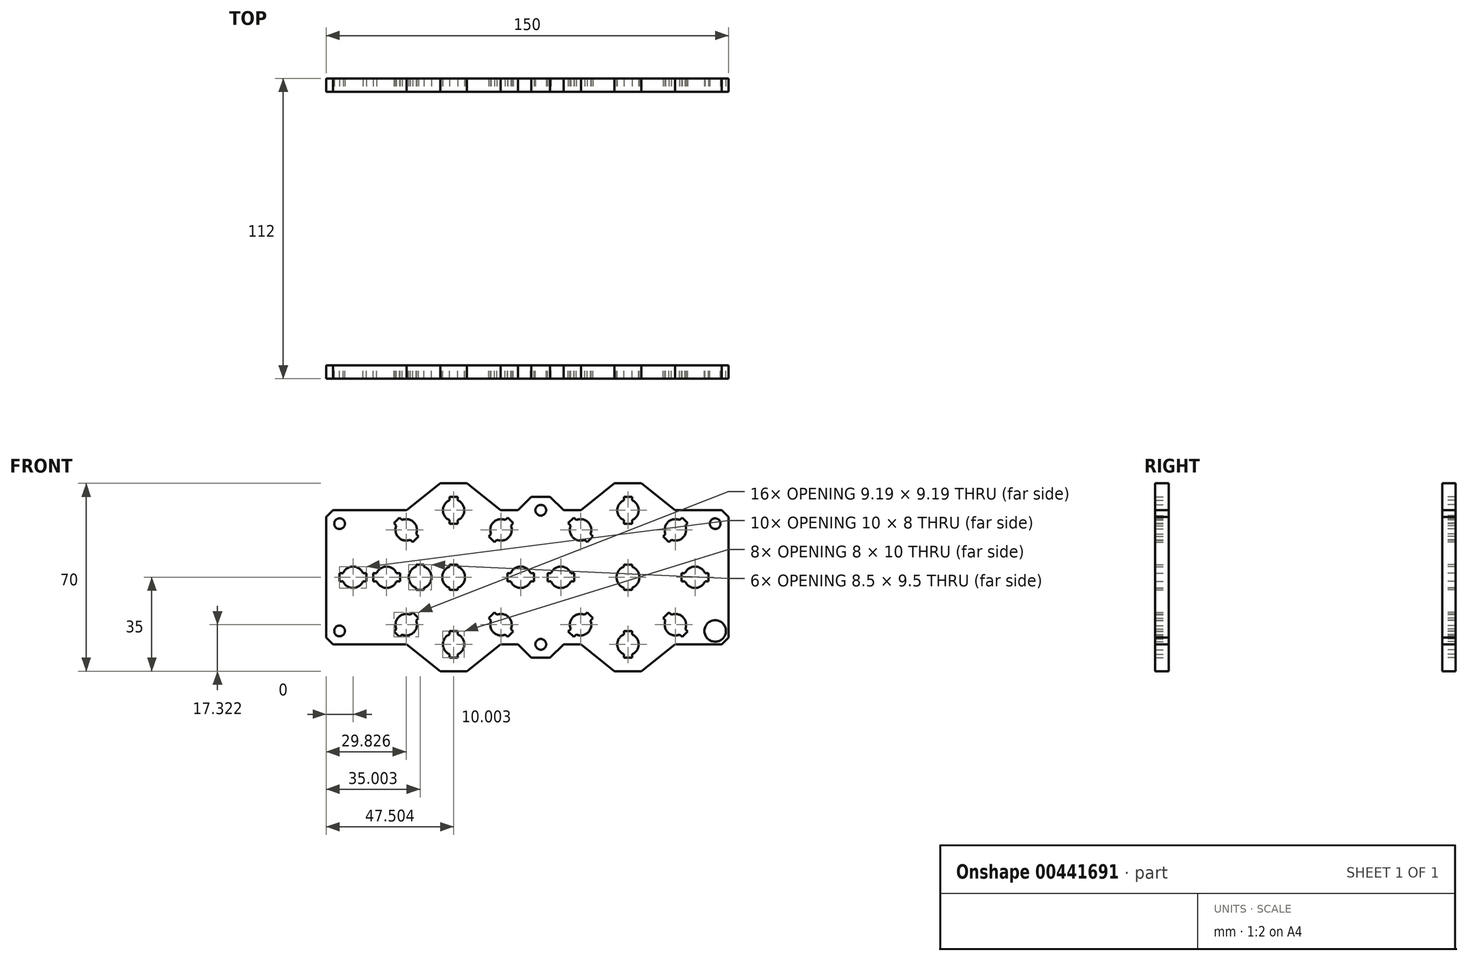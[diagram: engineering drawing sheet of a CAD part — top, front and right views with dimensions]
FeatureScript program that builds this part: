
annotation { "Feature Type Name" : "Feature", "Feature Type Description" : "" }
export const myFeature = defineFeature(function(context is Context, id is Id, definition is map)
    precondition{}
    {
        {
            var Q0;
            Q0=qCreatedBy(makeId("Front.planeOp"),FACE);
            var sketch = newSketch(context, id + "F0", { "sketchPlane" : qUnion([Q0])});
            skLineSegment(sketch, "E0", {"start": v(-68.44, 0) * mm, "end": v(-68.44, 25) * mm});
            skLineSegment(sketch, "E1", {"start": v(-68.44, 25) * mm, "end": v(-38.44, 25) * mm});
            skLineSegment(sketch, "E2", {"start": v(-38.44, 25) * mm, "end": v(-25.94, 35) * mm});
            skLineSegment(sketch, "E3", {"start": v(-25.94, 35) * mm, "end": v(-15.94, 35) * mm});
            skLineSegment(sketch, "E4", {"start": v(-15.94, 35) * mm, "end": v(-3.44, 25) * mm});
            skLineSegment(sketch, "E5", {"start": v(-3.44, 25) * mm, "end": v(26.56, 25) * mm});
            skLineSegment(sketch, "E6", {"start": v(26.56, 25) * mm, "end": v(39.06, 35) * mm});
            skLineSegment(sketch, "E7", {"start": v(39.06, 35) * mm, "end": v(49.06, 35) * mm});
            skLineSegment(sketch, "E8", {"start": v(49.06, 35) * mm, "end": v(61.56, 25) * mm});
            skLineSegment(sketch, "E9", {"start": v(61.56, 25) * mm, "end": v(81.56, 25) * mm});
            skLineSegment(sketch, "E10", {"start": v(81.56, 25) * mm, "end": v(81.56, 0) * mm});
            skLineSegment(sketch, "E11", {"start": v(-20.94, 68.31) * mm, "end": v(-20.94, -69.34) * mm, "construction": true});
            skLineSegment(sketch, "E12", {"start": v(44.06, 67.89) * mm, "end": v(44.06, -61.73) * mm, "construction": true});
            skLineSegment(sketch, "E13", {"start": v(87.46, 0) * mm, "end": v(-83.25, 0) * mm, "construction": true});
            skCircle(sketch, "E14", {"center": v(-20.94, 25) * mm, "radius": 4 * mm});
            skCircle(sketch, "E15", {"center": v(-20.94, 0) * mm, "radius": 25 * mm, "construction": true});
            skLineSegment(sketch, "E16", {"start": v(11.56, 59.14) * mm, "end": v(11.56, -51.84) * mm, "construction": true});
            skCircle(sketch, "E17.MirrorC", {"center": v(44.06, 0) * mm, "radius": 25 * mm, "construction": true});
            skCircle(sketch, "E18.MirrorC", {"center": v(44.06, 25) * mm, "radius": 4 * mm});
            skCircle(sketch, "E19.1.0", {"center": v(-38.61, 17.68) * mm, "radius": 4 * mm});
            skCircle(sketch, "E19.2.0", {"center": v(-45.94, 0) * mm, "radius": 4 * mm});
            skCircle(sketch, "E19.3.0", {"center": v(-38.61, -17.68) * mm, "radius": 4 * mm});
            skCircle(sketch, "E19.4.0", {"center": v(-20.94, -25) * mm, "radius": 4 * mm});
            skCircle(sketch, "E19.5.0", {"center": v(-3.26, -17.68) * mm, "radius": 4 * mm});
            skCircle(sketch, "E19.6.0", {"center": v(4.06, 0) * mm, "radius": 4 * mm});
            skCircle(sketch, "E19.7.0", {"center": v(-3.26, 17.68) * mm, "radius": 4 * mm});
            skCircle(sketch, "E20.MirrorC", {"center": v(61.74, 17.68) * mm, "radius": 4 * mm});
            skCircle(sketch, "E21.MirrorC", {"center": v(69.06, 0) * mm, "radius": 4 * mm});
            skCircle(sketch, "E22.MirrorC", {"center": v(61.74, -17.68) * mm, "radius": 4 * mm});
            skCircle(sketch, "E23.MirrorC", {"center": v(44.06, -25) * mm, "radius": 4 * mm});
            skCircle(sketch, "E24.MirrorC", {"center": v(26.39, -17.68) * mm, "radius": 4 * mm});
            skCircle(sketch, "E25.MirrorC", {"center": v(19.06, 0) * mm, "radius": 4 * mm});
            skCircle(sketch, "E26.MirrorC", {"center": v(26.39, 17.68) * mm, "radius": 4 * mm});
            skLineSegment(sketch, "E27.bottom", {"start": v(-22.44, 30) * mm, "end": v(-19.44, 30) * mm});
            skLineSegment(sketch, "E27.top", {"start": v(-22.44, 20) * mm, "end": v(-19.44, 20) * mm});
            skLineSegment(sketch, "E27.left", {"start": v(-22.44, 30) * mm, "end": v(-22.44, 20) * mm});
            skLineSegment(sketch, "E27.right", {"start": v(-19.44, 30) * mm, "end": v(-19.44, 20) * mm});
            skLineSegment(sketch, "E28", {"start": v(-32.15, 25) * mm, "end": v(-5.88, 25) * mm, "construction": true});
            skLineSegment(sketch, "E29.1.0", {"start": v(-43.21, 20.15) * mm, "end": v(-41.09, 22.27) * mm});
            skLineSegment(sketch, "E29.1.1", {"start": v(-43.21, 20.15) * mm, "end": v(-36.14, 13.08) * mm});
            skLineSegment(sketch, "E29.1.2", {"start": v(-36.14, 13.08) * mm, "end": v(-34.02, 15.2) * mm});
            skLineSegment(sketch, "E29.1.3", {"start": v(-41.09, 22.27) * mm, "end": v(-34.02, 15.2) * mm});
            skLineSegment(sketch, "E29.2.0", {"start": v(-50.94, -1.5) * mm, "end": v(-50.94, 1.5) * mm});
            skLineSegment(sketch, "E29.2.1", {"start": v(-50.94, -1.5) * mm, "end": v(-40.94, -1.5) * mm});
            skLineSegment(sketch, "E29.2.2", {"start": v(-40.94, -1.5) * mm, "end": v(-40.94, 1.5) * mm});
            skLineSegment(sketch, "E29.2.3", {"start": v(-50.94, 1.5) * mm, "end": v(-40.94, 1.5) * mm});
            skLineSegment(sketch, "E29.3.0", {"start": v(-41.09, -22.27) * mm, "end": v(-43.21, -20.15) * mm});
            skLineSegment(sketch, "E29.3.1", {"start": v(-41.09, -22.27) * mm, "end": v(-34.02, -15.2) * mm});
            skLineSegment(sketch, "E29.3.2", {"start": v(-34.02, -15.2) * mm, "end": v(-36.14, -13.08) * mm});
            skLineSegment(sketch, "E29.3.3", {"start": v(-43.21, -20.15) * mm, "end": v(-36.14, -13.08) * mm});
            skLineSegment(sketch, "E29.4.0", {"start": v(-19.44, -30) * mm, "end": v(-22.44, -30) * mm});
            skLineSegment(sketch, "E29.4.1", {"start": v(-19.44, -30) * mm, "end": v(-19.44, -20) * mm});
            skLineSegment(sketch, "E29.4.2", {"start": v(-19.44, -20) * mm, "end": v(-22.44, -20) * mm});
            skLineSegment(sketch, "E29.4.3", {"start": v(-22.44, -30) * mm, "end": v(-22.44, -20) * mm});
            skLineSegment(sketch, "E29.5.0", {"start": v(1.34, -20.15) * mm, "end": v(-0.78, -22.27) * mm});
            skLineSegment(sketch, "E29.5.1", {"start": v(1.34, -20.15) * mm, "end": v(-5.73, -13.08) * mm});
            skLineSegment(sketch, "E29.5.2", {"start": v(-5.73, -13.08) * mm, "end": v(-7.85, -15.2) * mm});
            skLineSegment(sketch, "E29.5.3", {"start": v(-0.78, -22.27) * mm, "end": v(-7.85, -15.2) * mm});
            skLineSegment(sketch, "E29.6.0", {"start": v(9.06, 1.5) * mm, "end": v(9.06, -1.5) * mm});
            skLineSegment(sketch, "E29.6.1", {"start": v(9.06, 1.5) * mm, "end": v(-0.94, 1.5) * mm});
            skLineSegment(sketch, "E29.6.2", {"start": v(-0.94, 1.5) * mm, "end": v(-0.94, -1.5) * mm});
            skLineSegment(sketch, "E29.6.3", {"start": v(9.06, -1.5) * mm, "end": v(-0.94, -1.5) * mm});
            skLineSegment(sketch, "E29.7.0", {"start": v(-0.78, 22.27) * mm, "end": v(1.34, 20.15) * mm});
            skLineSegment(sketch, "E29.7.1", {"start": v(-0.78, 22.27) * mm, "end": v(-7.85, 15.2) * mm});
            skLineSegment(sketch, "E29.7.2", {"start": v(-7.85, 15.2) * mm, "end": v(-5.73, 13.08) * mm});
            skLineSegment(sketch, "E29.7.3", {"start": v(1.34, 20.15) * mm, "end": v(-5.73, 13.08) * mm});
            skLineSegment(sketch, "E30.MirrorCS", {"start": v(45.56, 30) * mm, "end": v(42.56, 30) * mm});
            skLineSegment(sketch, "E31.MirrorCS", {"start": v(45.56, 30) * mm, "end": v(45.56, 20) * mm});
            skLineSegment(sketch, "E32.MirrorCS", {"start": v(45.56, 20) * mm, "end": v(42.56, 20) * mm});
            skLineSegment(sketch, "E33.MirrorCS", {"start": v(42.56, 30) * mm, "end": v(42.56, 20) * mm});
            skLineSegment(sketch, "E34.MirrorCS", {"start": v(23.91, 22.27) * mm, "end": v(30.98, 15.2) * mm});
            skLineSegment(sketch, "E35.MirrorCS", {"start": v(21.79, 20.15) * mm, "end": v(28.86, 13.08) * mm});
            skLineSegment(sketch, "E36.MirrorCS", {"start": v(30.98, 15.2) * mm, "end": v(28.86, 13.08) * mm});
            skLineSegment(sketch, "E37.MirrorCS", {"start": v(23.91, 22.27) * mm, "end": v(21.79, 20.15) * mm});
            skLineSegment(sketch, "E38.MirrorCS", {"start": v(-68.44, 0) * mm, "end": v(-68.44, -25) * mm});
            skLineSegment(sketch, "E39.MirrorCS", {"start": v(-68.44, -25) * mm, "end": v(-38.44, -25) * mm});
            skLineSegment(sketch, "E40.MirrorCS", {"start": v(-38.44, -25) * mm, "end": v(-25.94, -35) * mm});
            skLineSegment(sketch, "E41.MirrorCS", {"start": v(-25.94, -35) * mm, "end": v(-15.94, -35) * mm});
            skLineSegment(sketch, "E42.MirrorCS", {"start": v(-15.94, -35) * mm, "end": v(-3.44, -25) * mm});
            skLineSegment(sketch, "E43.MirrorCS", {"start": v(-3.44, -25) * mm, "end": v(26.56, -25) * mm});
            skLineSegment(sketch, "E44.MirrorCS", {"start": v(26.56, -25) * mm, "end": v(39.06, -35) * mm});
            skLineSegment(sketch, "E45.MirrorCS", {"start": v(39.06, -35) * mm, "end": v(49.06, -35) * mm});
            skLineSegment(sketch, "E46.MirrorCS", {"start": v(49.06, -35) * mm, "end": v(61.56, -25) * mm});
            skLineSegment(sketch, "E47.MirrorCS", {"start": v(61.56, -25) * mm, "end": v(81.56, -25) * mm});
            skLineSegment(sketch, "E48.MirrorCS", {"start": v(81.56, -25) * mm, "end": v(81.56, 0) * mm});
            skLineSegment(sketch, "E49.MirrorCS", {"start": v(14.06, 1.5) * mm, "end": v(24.06, 1.5) * mm});
            skLineSegment(sketch, "E50.MirrorCS", {"start": v(14.06, -1.5) * mm, "end": v(24.06, -1.5) * mm});
            skLineSegment(sketch, "E51.MirrorCS", {"start": v(14.06, 1.5) * mm, "end": v(14.06, -1.5) * mm});
            skLineSegment(sketch, "E52.MirrorCS", {"start": v(24.06, 1.5) * mm, "end": v(24.06, -1.5) * mm});
            skLineSegment(sketch, "E53.MirrorCS", {"start": v(28.86, -13.08) * mm, "end": v(30.98, -15.2) * mm});
            skLineSegment(sketch, "E54.MirrorCS", {"start": v(23.91, -22.27) * mm, "end": v(30.98, -15.2) * mm});
            skLineSegment(sketch, "E55.MirrorCS", {"start": v(21.79, -20.15) * mm, "end": v(28.86, -13.08) * mm});
            skLineSegment(sketch, "E56.MirrorCS", {"start": v(21.79, -20.15) * mm, "end": v(23.91, -22.27) * mm});
            skLineSegment(sketch, "E57.MirrorCS", {"start": v(42.56, -30) * mm, "end": v(45.56, -30) * mm});
            skLineSegment(sketch, "E58.MirrorCS", {"start": v(45.56, -30) * mm, "end": v(45.56, -20) * mm});
            skLineSegment(sketch, "E59.MirrorCS", {"start": v(42.56, -20) * mm, "end": v(45.56, -20) * mm});
            skLineSegment(sketch, "E60.MirrorCS", {"start": v(42.56, -30) * mm, "end": v(42.56, -20) * mm});
            skLineSegment(sketch, "E61.MirrorCS", {"start": v(64.22, -22.27) * mm, "end": v(57.15, -15.2) * mm});
            skLineSegment(sketch, "E62.MirrorCS", {"start": v(66.34, -20.15) * mm, "end": v(59.27, -13.08) * mm});
            skLineSegment(sketch, "E63.MirrorCS", {"start": v(64.22, -22.27) * mm, "end": v(66.34, -20.15) * mm});
            skLineSegment(sketch, "E64.MirrorCS", {"start": v(57.15, -15.2) * mm, "end": v(59.27, -13.08) * mm});
            skLineSegment(sketch, "E65.MirrorCS", {"start": v(74.06, -1.5) * mm, "end": v(64.06, -1.5) * mm});
            skLineSegment(sketch, "E66.MirrorCS", {"start": v(74.06, 1.5) * mm, "end": v(64.06, 1.5) * mm});
            skLineSegment(sketch, "E67.MirrorCS", {"start": v(64.06, -1.5) * mm, "end": v(64.06, 1.5) * mm});
            skLineSegment(sketch, "E68.MirrorCS", {"start": v(74.06, -1.5) * mm, "end": v(74.06, 1.5) * mm});
            skLineSegment(sketch, "E69.MirrorCS", {"start": v(59.27, 13.08) * mm, "end": v(57.15, 15.2) * mm});
            skLineSegment(sketch, "E70.MirrorCS", {"start": v(64.22, 22.27) * mm, "end": v(57.15, 15.2) * mm});
            skLineSegment(sketch, "E71.MirrorCS", {"start": v(66.34, 20.15) * mm, "end": v(59.27, 13.08) * mm});
            skLineSegment(sketch, "E72.MirrorCS", {"start": v(66.34, 20.15) * mm, "end": v(64.22, 22.27) * mm});
            skCircle(sketch, "E73", {"center": v(-20.94, 0) * mm, "radius": 4.25 * mm});
            skCircle(sketch, "E74.MirrorC", {"center": v(44.06, 0) * mm, "radius": 4.25 * mm});
            skLineSegment(sketch, "E75", {"start": v(-8.74, 7.5) * mm, "end": v(-8.74, -9.58) * mm, "construction": true});
            skLineSegment(sketch, "E76", {"start": v(-33.44, 7.24) * mm, "end": v(-33.44, -7.43) * mm, "construction": true});
            skCircle(sketch, "E77.MirrorC", {"center": v(-58.44, 0) * mm, "radius": 4 * mm});
            skCircle(sketch, "E78", {"center": v(76.56, 20) * mm, "radius": 4 * mm});
            skCircle(sketch, "E79", {"center": v(76.56, 20) * mm, "radius": 2 * mm});
            skCircle(sketch, "E80.MirrorC", {"center": v(76.56, -20) * mm, "radius": 4 * mm});
            skCircle(sketch, "E81.MirrorC", {"center": v(76.56, -20) * mm, "radius": 2 * mm});
            skCircle(sketch, "E82", {"center": v(-63.44, 20) * mm, "radius": 2 * mm});
            skCircle(sketch, "E83.MirrorC", {"center": v(-63.44, -20) * mm, "radius": 2 * mm});
            skCircle(sketch, "E84", {"center": v(11.56, 25) * mm, "radius": 2 * mm});
            skCircle(sketch, "E85.MirrorC", {"center": v(11.56, -25) * mm, "radius": 2 * mm});
            skLineSegment(sketch, "E86", {"start": v(3.06, 25) * mm, "end": v(8.06, 30) * mm});
            skLineSegment(sketch, "E87", {"start": v(8.06, 30) * mm, "end": v(15.06, 30) * mm});
            skLineSegment(sketch, "E88", {"start": v(15.06, 30) * mm, "end": v(20.06, 25) * mm});
            skLineSegment(sketch, "E89.MirrorCS", {"start": v(3.06, -25) * mm, "end": v(8.06, -30) * mm});
            skLineSegment(sketch, "E90.MirrorCS", {"start": v(8.06, -30) * mm, "end": v(15.06, -30) * mm});
            skLineSegment(sketch, "E91.MirrorCS", {"start": v(15.06, -30) * mm, "end": v(20.06, -25) * mm});
            skCircle(sketch, "E92", {"center": v(-33.44, 0) * mm, "radius": 4.25 * mm});
            skLineSegment(sketch, "E93", {"start": v(-19.44, 4.75) * mm, "end": v(-19.44, -4.75) * mm});
            skLineSegment(sketch, "E94", {"start": v(-19.44, -4.75) * mm, "end": v(-22.44, -4.75) * mm});
            skLineSegment(sketch, "E95", {"start": v(-22.44, -4.75) * mm, "end": v(-22.44, 4.75) * mm});
            skLineSegment(sketch, "E96", {"start": v(-22.44, 4.75) * mm, "end": v(-19.44, 4.75) * mm});
            skLineSegment(sketch, "E97.MirrorCS", {"start": v(42.56, 4.75) * mm, "end": v(42.56, -4.75) * mm});
            skLineSegment(sketch, "E98.MirrorCS", {"start": v(45.56, -4.75) * mm, "end": v(45.56, 4.75) * mm});
            skLineSegment(sketch, "E99.MirrorCS", {"start": v(42.56, -4.75) * mm, "end": v(45.56, -4.75) * mm});
            skLineSegment(sketch, "E100.MirrorCS", {"start": v(45.56, 4.75) * mm, "end": v(42.56, 4.75) * mm});
            skLineSegment(sketch, "E101.MirrorCS", {"start": v(44.06, 68.31) * mm, "end": v(44.06, -69.34) * mm, "construction": true});
            skLineSegment(sketch, "E102", {"start": v(-33.44, 33.8) * mm, "end": v(-33.44, -30.95) * mm, "construction": true});
            skLineSegment(sketch, "E103", {"start": v(-58.44, 33.47) * mm, "end": v(-58.44, -35.83) * mm, "construction": true});
            skLineSegment(sketch, "E104.bottom", {"start": v(-63.44, 1.5) * mm, "end": v(-53.44, 1.5) * mm});
            skLineSegment(sketch, "E104.top", {"start": v(-63.44, -1.5) * mm, "end": v(-53.44, -1.5) * mm});
            skLineSegment(sketch, "E104.left", {"start": v(-63.44, 1.5) * mm, "end": v(-63.44, -1.5) * mm});
            skLineSegment(sketch, "E104.right", {"start": v(-53.44, 1.5) * mm, "end": v(-53.44, -1.5) * mm});
            skLineSegment(sketch, "E105.bottom", {"start": v(-34.94, 4.75) * mm, "end": v(-31.94, 4.75) * mm});
            skLineSegment(sketch, "E105.top", {"start": v(-34.94, -4.75) * mm, "end": v(-31.94, -4.75) * mm});
            skLineSegment(sketch, "E105.left", {"start": v(-34.94, 4.75) * mm, "end": v(-34.94, -4.75) * mm});
            skLineSegment(sketch, "E105.right", {"start": v(-31.94, 4.75) * mm, "end": v(-31.94, -4.75) * mm});
            skSolve(sketch);
        }
        {
            var Q0;
            Q0=makeQuery(id+"F0.imprint","IMPRINT",FACE,{"disambiguationData":[TD([[makeQuery(id+"F0.imprint","IMPRINT",EDGE,{"derivedFrom":sQuery(id+"F0.wireOp",EDGE,"E78")}),1.0]])]});
            var Q1;
            Q1=makeQuery(id+"F0.imprint","IMPRINT",FACE,{"disambiguationData":[TD([[makeQuery(id+"F0.imprint","IMPRINT",EDGE,{"derivedFrom":sQuery(id+"F0.wireOp",EDGE,"E0")}),-1.0]])]});
            var Q2;
            Q2=makeQuery(id+"F0.imprint","IMPRINT",FACE,{"disambiguationData":[TD([[makeQuery(id+"F0.imprint","IMPRINT",EDGE,{"derivedFrom":sQuery(id+"F0.wireOp",EDGE,"E80.MirrorC")}),-1.0]])]});
            var Q3;
            {var subQ0=sQuery(id+"F0.wireOp",EDGE,"E86");Q3=makeQuery(id+"F0.imprint","IMPRINT",FACE,{"disambiguationData":[TD([[makeQuery(id+"F0.imprint","IMPRINT",EDGE,{"derivedFrom":subQ0}),-1.0]])]});}
            var Q4;
            {var subQ0=sQuery(id+"F0.wireOp",EDGE,"E89.MirrorCS");Q4=makeQuery(id+"F0.imprint","IMPRINT",FACE,{"disambiguationData":[TD([[makeQuery(id+"F0.imprint","IMPRINT",EDGE,{"derivedFrom":subQ0}),1.0]])]});}
            extrude(context, id + "F1", {"entities" : qUnion([Q0, Q1, Q2, Q3, Q4]), "endBound" : BoundingType.SYMMETRIC, "depth" : 5 * mm});
        }
        {
            var Q0;
            Q0=makeQuery(id+"F1.opExtrude","SWEPT_EDGE",EDGE,{"disambiguationData":[OSD([sQuery(id+"F0.wireOp",EDGE,"E9"),sQuery(id+"F0.wireOp",EDGE,"E10")])]});
            var Q1;
            Q1=makeQuery(id+"F1.opExtrude","SWEPT_EDGE",EDGE,{"disambiguationData":[OSD([sQuery(id+"F0.wireOp",EDGE,"E47.MirrorCS"),sQuery(id+"F0.wireOp",EDGE,"E48.MirrorCS")])]});
            var Q2;
            Q2=makeQuery(id+"F1.opExtrude","SWEPT_EDGE",EDGE,{"disambiguationData":[OSD([sQuery(id+"F0.wireOp",EDGE,"E0"),sQuery(id+"F0.wireOp",EDGE,"E1")])]});
            var Q3;
            Q3=makeQuery(id+"F1.opExtrude","SWEPT_EDGE",EDGE,{"disambiguationData":[OSD([sQuery(id+"F0.wireOp",EDGE,"E38.MirrorCS"),sQuery(id+"F0.wireOp",EDGE,"E39.MirrorCS")])]});
            chamfer(context, id + "F2", {"entities" : qUnion([Q0, Q1, Q2, Q3]), "width" : 2.5 * mm, "tangentPropagation" : true});
        }
        {
            var Q0;
            Q0=makeQuery(id+"F1.opExtrude","CAP_FACE",FACE,{"disambiguationData":[OSD([sQuery(id+"F0.wireOp",EDGE,"E0"),sQuery(id+"F0.wireOp",EDGE,"E1"),sQuery(id+"F0.wireOp",EDGE,"E2"),sQuery(id+"F0.wireOp",EDGE,"E3"),sQuery(id+"F0.wireOp",EDGE,"E4"),sQuery(id+"F0.wireOp",EDGE,"E5"),sQuery(id+"F0.wireOp",EDGE,"E6"),sQuery(id+"F0.wireOp",EDGE,"E7"),sQuery(id+"F0.wireOp",EDGE,"E8"),sQuery(id+"F0.wireOp",EDGE,"E9"),sQuery(id+"F0.wireOp",EDGE,"E10"),sQuery(id+"F0.wireOp",EDGE,"E14"),sQuery(id+"F0.wireOp",EDGE,"E18.MirrorC"),sQuery(id+"F0.wireOp",EDGE,"E19.1.0"),sQuery(id+"F0.wireOp",EDGE,"E19.2.0"),sQuery(id+"F0.wireOp",EDGE,"E19.3.0"),sQuery(id+"F0.wireOp",EDGE,"E19.4.0"),sQuery(id+"F0.wireOp",EDGE,"E19.5.0"),sQuery(id+"F0.wireOp",EDGE,"E19.6.0"),sQuery(id+"F0.wireOp",EDGE,"E19.7.0"),sQuery(id+"F0.wireOp",EDGE,"E20.MirrorC"),sQuery(id+"F0.wireOp",EDGE,"E21.MirrorC"),sQuery(id+"F0.wireOp",EDGE,"E22.MirrorC"),sQuery(id+"F0.wireOp",EDGE,"E23.MirrorC"),sQuery(id+"F0.wireOp",EDGE,"E24.MirrorC"),sQuery(id+"F0.wireOp",EDGE,"E25.MirrorC"),sQuery(id+"F0.wireOp",EDGE,"E26.MirrorC"),sQuery(id+"F0.wireOp",EDGE,"E27.bottom"),sQuery(id+"F0.wireOp",EDGE,"E27.top"),sQuery(id+"F0.wireOp",EDGE,"E27.left"),sQuery(id+"F0.wireOp",EDGE,"E27.right"),sQuery(id+"F0.wireOp",EDGE,"E29.1.0"),sQuery(id+"F0.wireOp",EDGE,"E29.1.1"),sQuery(id+"F0.wireOp",EDGE,"E29.1.2"),sQuery(id+"F0.wireOp",EDGE,"E29.1.3"),sQuery(id+"F0.wireOp",EDGE,"E29.2.0"),sQuery(id+"F0.wireOp",EDGE,"E29.2.1"),sQuery(id+"F0.wireOp",EDGE,"E29.2.2"),sQuery(id+"F0.wireOp",EDGE,"E29.2.3"),sQuery(id+"F0.wireOp",EDGE,"E29.3.0"),sQuery(id+"F0.wireOp",EDGE,"E29.3.1"),sQuery(id+"F0.wireOp",EDGE,"E29.3.2"),sQuery(id+"F0.wireOp",EDGE,"E29.3.3"),sQuery(id+"F0.wireOp",EDGE,"E29.4.0"),sQuery(id+"F0.wireOp",EDGE,"E29.4.1"),sQuery(id+"F0.wireOp",EDGE,"E29.4.2"),sQuery(id+"F0.wireOp",EDGE,"E29.4.3"),sQuery(id+"F0.wireOp",EDGE,"E29.5.0"),sQuery(id+"F0.wireOp",EDGE,"E29.5.1"),sQuery(id+"F0.wireOp",EDGE,"E29.5.2"),sQuery(id+"F0.wireOp",EDGE,"E29.5.3"),sQuery(id+"F0.wireOp",EDGE,"E29.6.0"),sQuery(id+"F0.wireOp",EDGE,"E29.6.1"),sQuery(id+"F0.wireOp",EDGE,"E29.6.2"),sQuery(id+"F0.wireOp",EDGE,"E29.6.3"),sQuery(id+"F0.wireOp",EDGE,"E29.7.0"),sQuery(id+"F0.wireOp",EDGE,"E29.7.1"),sQuery(id+"F0.wireOp",EDGE,"E29.7.2"),sQuery(id+"F0.wireOp",EDGE,"E29.7.3"),sQuery(id+"F0.wireOp",EDGE,"E30.MirrorCS"),sQuery(id+"F0.wireOp",EDGE,"E31.MirrorCS"),sQuery(id+"F0.wireOp",EDGE,"E32.MirrorCS"),sQuery(id+"F0.wireOp",EDGE,"E33.MirrorCS"),sQuery(id+"F0.wireOp",EDGE,"E34.MirrorCS"),sQuery(id+"F0.wireOp",EDGE,"E35.MirrorCS"),sQuery(id+"F0.wireOp",EDGE,"E36.MirrorCS"),sQuery(id+"F0.wireOp",EDGE,"E37.MirrorCS"),sQuery(id+"F0.wireOp",EDGE,"E38.MirrorCS"),sQuery(id+"F0.wireOp",EDGE,"E39.MirrorCS"),sQuery(id+"F0.wireOp",EDGE,"E40.MirrorCS"),sQuery(id+"F0.wireOp",EDGE,"E41.MirrorCS"),sQuery(id+"F0.wireOp",EDGE,"E42.MirrorCS"),sQuery(id+"F0.wireOp",EDGE,"E43.MirrorCS"),sQuery(id+"F0.wireOp",EDGE,"E44.MirrorCS"),sQuery(id+"F0.wireOp",EDGE,"E45.MirrorCS"),sQuery(id+"F0.wireOp",EDGE,"E46.MirrorCS"),sQuery(id+"F0.wireOp",EDGE,"E47.MirrorCS"),sQuery(id+"F0.wireOp",EDGE,"E48.MirrorCS"),sQuery(id+"F0.wireOp",EDGE,"E49.MirrorCS"),sQuery(id+"F0.wireOp",EDGE,"E50.MirrorCS"),sQuery(id+"F0.wireOp",EDGE,"E51.MirrorCS"),sQuery(id+"F0.wireOp",EDGE,"E52.MirrorCS"),sQuery(id+"F0.wireOp",EDGE,"E53.MirrorCS"),sQuery(id+"F0.wireOp",EDGE,"E54.MirrorCS"),sQuery(id+"F0.wireOp",EDGE,"E55.MirrorCS"),sQuery(id+"F0.wireOp",EDGE,"E56.MirrorCS"),sQuery(id+"F0.wireOp",EDGE,"E57.MirrorCS"),sQuery(id+"F0.wireOp",EDGE,"E58.MirrorCS"),sQuery(id+"F0.wireOp",EDGE,"E59.MirrorCS"),sQuery(id+"F0.wireOp",EDGE,"E60.MirrorCS"),sQuery(id+"F0.wireOp",EDGE,"E61.MirrorCS"),sQuery(id+"F0.wireOp",EDGE,"E62.MirrorCS"),sQuery(id+"F0.wireOp",EDGE,"E63.MirrorCS"),sQuery(id+"F0.wireOp",EDGE,"E64.MirrorCS"),sQuery(id+"F0.wireOp",EDGE,"E65.MirrorCS"),sQuery(id+"F0.wireOp",EDGE,"E66.MirrorCS"),sQuery(id+"F0.wireOp",EDGE,"E67.MirrorCS"),sQuery(id+"F0.wireOp",EDGE,"E68.MirrorCS"),sQuery(id+"F0.wireOp",EDGE,"E69.MirrorCS"),sQuery(id+"F0.wireOp",EDGE,"E70.MirrorCS"),sQuery(id+"F0.wireOp",EDGE,"E71.MirrorCS"),sQuery(id+"F0.wireOp",EDGE,"E72.MirrorCS"),sQuery(id+"F0.wireOp",EDGE,"E73"),sQuery(id+"F0.wireOp",EDGE,"E74.MirrorC"),sQuery(id+"F0.wireOp",EDGE,"E77.MirrorC"),sQuery(id+"F0.wireOp",EDGE,"E79"),sQuery(id+"F0.wireOp",EDGE,"E81.MirrorC"),sQuery(id+"F0.wireOp",EDGE,"E82"),sQuery(id+"F0.wireOp",EDGE,"E83.MirrorC"),sQuery(id+"F0.wireOp",EDGE,"E84"),sQuery(id+"F0.wireOp",EDGE,"E85.MirrorC"),sQuery(id+"F0.wireOp",EDGE,"E86"),sQuery(id+"F0.wireOp",EDGE,"E87"),sQuery(id+"F0.wireOp",EDGE,"E88"),sQuery(id+"F0.wireOp",EDGE,"E89.MirrorCS"),sQuery(id+"F0.wireOp",EDGE,"E90.MirrorCS"),sQuery(id+"F0.wireOp",EDGE,"E91.MirrorCS"),sQuery(id+"F0.wireOp",EDGE,"E92"),sQuery(id+"F0.wireOp",EDGE,"E93"),sQuery(id+"F0.wireOp",EDGE,"E94"),sQuery(id+"F0.wireOp",EDGE,"E95"),sQuery(id+"F0.wireOp",EDGE,"E96"),sQuery(id+"F0.wireOp",EDGE,"E98.MirrorCS"),sQuery(id+"F0.wireOp",EDGE,"E97.MirrorCS"),sQuery(id+"F0.wireOp",EDGE,"E99.MirrorCS"),sQuery(id+"F0.wireOp",EDGE,"E100.MirrorCS"),sQuery(id+"F0.wireOp",EDGE,"E104.bottom"),sQuery(id+"F0.wireOp",EDGE,"E104.top"),sQuery(id+"F0.wireOp",EDGE,"E104.left"),sQuery(id+"F0.wireOp",EDGE,"E104.right"),sQuery(id+"F0.wireOp",EDGE,"E105.bottom"),sQuery(id+"F0.wireOp",EDGE,"E105.top"),sQuery(id+"F0.wireOp",EDGE,"E105.left"),sQuery(id+"F0.wireOp",EDGE,"E105.right")])],"isStart":true});
            cPlane(context, id + "F3", {"entities" : qUnion([Q0]), "cplaneType" : CPlaneType.OFFSET, "offset" : (102 / 2) * mm, "width" : 150 * mm, "height" : 150 * mm});
        }
        {
            var Q0;
            Q0=makeQuery(id+"F1.opExtrude","SWEPT_BODY",BODY,{"disambiguationData":[OSD([sQuery(id+"F0.wireOp",EDGE,"E0"),sQuery(id+"F0.wireOp",EDGE,"E1"),sQuery(id+"F0.wireOp",EDGE,"E2"),sQuery(id+"F0.wireOp",EDGE,"E3"),sQuery(id+"F0.wireOp",EDGE,"E4"),sQuery(id+"F0.wireOp",EDGE,"E5"),sQuery(id+"F0.wireOp",EDGE,"E6"),sQuery(id+"F0.wireOp",EDGE,"E7"),sQuery(id+"F0.wireOp",EDGE,"E8"),sQuery(id+"F0.wireOp",EDGE,"E9"),sQuery(id+"F0.wireOp",EDGE,"E10"),sQuery(id+"F0.wireOp",EDGE,"E14"),sQuery(id+"F0.wireOp",EDGE,"E18.MirrorC"),sQuery(id+"F0.wireOp",EDGE,"E19.1.0"),sQuery(id+"F0.wireOp",EDGE,"E19.2.0"),sQuery(id+"F0.wireOp",EDGE,"E19.3.0"),sQuery(id+"F0.wireOp",EDGE,"E19.4.0"),sQuery(id+"F0.wireOp",EDGE,"E19.5.0"),sQuery(id+"F0.wireOp",EDGE,"E19.6.0"),sQuery(id+"F0.wireOp",EDGE,"E19.7.0"),sQuery(id+"F0.wireOp",EDGE,"E20.MirrorC"),sQuery(id+"F0.wireOp",EDGE,"E21.MirrorC"),sQuery(id+"F0.wireOp",EDGE,"E22.MirrorC"),sQuery(id+"F0.wireOp",EDGE,"E23.MirrorC"),sQuery(id+"F0.wireOp",EDGE,"E24.MirrorC"),sQuery(id+"F0.wireOp",EDGE,"E25.MirrorC"),sQuery(id+"F0.wireOp",EDGE,"E26.MirrorC"),sQuery(id+"F0.wireOp",EDGE,"E27.bottom"),sQuery(id+"F0.wireOp",EDGE,"E27.top"),sQuery(id+"F0.wireOp",EDGE,"E27.left"),sQuery(id+"F0.wireOp",EDGE,"E27.right"),sQuery(id+"F0.wireOp",EDGE,"E29.1.0"),sQuery(id+"F0.wireOp",EDGE,"E29.1.1"),sQuery(id+"F0.wireOp",EDGE,"E29.1.2"),sQuery(id+"F0.wireOp",EDGE,"E29.1.3"),sQuery(id+"F0.wireOp",EDGE,"E29.2.0"),sQuery(id+"F0.wireOp",EDGE,"E29.2.1"),sQuery(id+"F0.wireOp",EDGE,"E29.2.2"),sQuery(id+"F0.wireOp",EDGE,"E29.2.3"),sQuery(id+"F0.wireOp",EDGE,"E29.3.0"),sQuery(id+"F0.wireOp",EDGE,"E29.3.1"),sQuery(id+"F0.wireOp",EDGE,"E29.3.2"),sQuery(id+"F0.wireOp",EDGE,"E29.3.3"),sQuery(id+"F0.wireOp",EDGE,"E29.4.0"),sQuery(id+"F0.wireOp",EDGE,"E29.4.1"),sQuery(id+"F0.wireOp",EDGE,"E29.4.2"),sQuery(id+"F0.wireOp",EDGE,"E29.4.3"),sQuery(id+"F0.wireOp",EDGE,"E29.5.0"),sQuery(id+"F0.wireOp",EDGE,"E29.5.1"),sQuery(id+"F0.wireOp",EDGE,"E29.5.2"),sQuery(id+"F0.wireOp",EDGE,"E29.5.3"),sQuery(id+"F0.wireOp",EDGE,"E29.6.0"),sQuery(id+"F0.wireOp",EDGE,"E29.6.1"),sQuery(id+"F0.wireOp",EDGE,"E29.6.2"),sQuery(id+"F0.wireOp",EDGE,"E29.6.3"),sQuery(id+"F0.wireOp",EDGE,"E29.7.0"),sQuery(id+"F0.wireOp",EDGE,"E29.7.1"),sQuery(id+"F0.wireOp",EDGE,"E29.7.2"),sQuery(id+"F0.wireOp",EDGE,"E29.7.3"),sQuery(id+"F0.wireOp",EDGE,"E30.MirrorCS"),sQuery(id+"F0.wireOp",EDGE,"E31.MirrorCS"),sQuery(id+"F0.wireOp",EDGE,"E32.MirrorCS"),sQuery(id+"F0.wireOp",EDGE,"E33.MirrorCS"),sQuery(id+"F0.wireOp",EDGE,"E34.MirrorCS"),sQuery(id+"F0.wireOp",EDGE,"E35.MirrorCS"),sQuery(id+"F0.wireOp",EDGE,"E36.MirrorCS"),sQuery(id+"F0.wireOp",EDGE,"E37.MirrorCS"),sQuery(id+"F0.wireOp",EDGE,"E38.MirrorCS"),sQuery(id+"F0.wireOp",EDGE,"E39.MirrorCS"),sQuery(id+"F0.wireOp",EDGE,"E40.MirrorCS"),sQuery(id+"F0.wireOp",EDGE,"E41.MirrorCS"),sQuery(id+"F0.wireOp",EDGE,"E42.MirrorCS"),sQuery(id+"F0.wireOp",EDGE,"E43.MirrorCS"),sQuery(id+"F0.wireOp",EDGE,"E44.MirrorCS"),sQuery(id+"F0.wireOp",EDGE,"E45.MirrorCS"),sQuery(id+"F0.wireOp",EDGE,"E46.MirrorCS"),sQuery(id+"F0.wireOp",EDGE,"E47.MirrorCS"),sQuery(id+"F0.wireOp",EDGE,"E48.MirrorCS"),sQuery(id+"F0.wireOp",EDGE,"E49.MirrorCS"),sQuery(id+"F0.wireOp",EDGE,"E50.MirrorCS"),sQuery(id+"F0.wireOp",EDGE,"E51.MirrorCS"),sQuery(id+"F0.wireOp",EDGE,"E52.MirrorCS"),sQuery(id+"F0.wireOp",EDGE,"E53.MirrorCS"),sQuery(id+"F0.wireOp",EDGE,"E54.MirrorCS"),sQuery(id+"F0.wireOp",EDGE,"E55.MirrorCS"),sQuery(id+"F0.wireOp",EDGE,"E56.MirrorCS"),sQuery(id+"F0.wireOp",EDGE,"E57.MirrorCS"),sQuery(id+"F0.wireOp",EDGE,"E58.MirrorCS"),sQuery(id+"F0.wireOp",EDGE,"E59.MirrorCS"),sQuery(id+"F0.wireOp",EDGE,"E60.MirrorCS"),sQuery(id+"F0.wireOp",EDGE,"E61.MirrorCS"),sQuery(id+"F0.wireOp",EDGE,"E62.MirrorCS"),sQuery(id+"F0.wireOp",EDGE,"E63.MirrorCS"),sQuery(id+"F0.wireOp",EDGE,"E64.MirrorCS"),sQuery(id+"F0.wireOp",EDGE,"E65.MirrorCS"),sQuery(id+"F0.wireOp",EDGE,"E66.MirrorCS"),sQuery(id+"F0.wireOp",EDGE,"E67.MirrorCS"),sQuery(id+"F0.wireOp",EDGE,"E68.MirrorCS"),sQuery(id+"F0.wireOp",EDGE,"E69.MirrorCS"),sQuery(id+"F0.wireOp",EDGE,"E70.MirrorCS"),sQuery(id+"F0.wireOp",EDGE,"E71.MirrorCS"),sQuery(id+"F0.wireOp",EDGE,"E72.MirrorCS"),sQuery(id+"F0.wireOp",EDGE,"E73"),sQuery(id+"F0.wireOp",EDGE,"E74.MirrorC"),sQuery(id+"F0.wireOp",EDGE,"E77.MirrorC"),sQuery(id+"F0.wireOp",EDGE,"E79"),sQuery(id+"F0.wireOp",EDGE,"E81.MirrorC"),sQuery(id+"F0.wireOp",EDGE,"E82"),sQuery(id+"F0.wireOp",EDGE,"E83.MirrorC"),sQuery(id+"F0.wireOp",EDGE,"E84"),sQuery(id+"F0.wireOp",EDGE,"E85.MirrorC"),sQuery(id+"F0.wireOp",EDGE,"E86"),sQuery(id+"F0.wireOp",EDGE,"E87"),sQuery(id+"F0.wireOp",EDGE,"E88"),sQuery(id+"F0.wireOp",EDGE,"E89.MirrorCS"),sQuery(id+"F0.wireOp",EDGE,"E90.MirrorCS"),sQuery(id+"F0.wireOp",EDGE,"E91.MirrorCS"),sQuery(id+"F0.wireOp",EDGE,"E92"),sQuery(id+"F0.wireOp",EDGE,"E93"),sQuery(id+"F0.wireOp",EDGE,"E94"),sQuery(id+"F0.wireOp",EDGE,"E95"),sQuery(id+"F0.wireOp",EDGE,"E96"),sQuery(id+"F0.wireOp",EDGE,"E98.MirrorCS"),sQuery(id+"F0.wireOp",EDGE,"E97.MirrorCS"),sQuery(id+"F0.wireOp",EDGE,"E99.MirrorCS"),sQuery(id+"F0.wireOp",EDGE,"E100.MirrorCS"),sQuery(id+"F0.wireOp",EDGE,"E104.bottom"),sQuery(id+"F0.wireOp",EDGE,"E104.top"),sQuery(id+"F0.wireOp",EDGE,"E104.left"),sQuery(id+"F0.wireOp",EDGE,"E104.right"),sQuery(id+"F0.wireOp",EDGE,"E105.bottom"),sQuery(id+"F0.wireOp",EDGE,"E105.top"),sQuery(id+"F0.wireOp",EDGE,"E105.left"),sQuery(id+"F0.wireOp",EDGE,"E105.right")])]});
            var Q1;
            Q1=qCreatedBy(id+"F3.planeOp",FACE);
            mirror(context, id + "F4", {"entities" : qUnion([Q0]), "mirrorPlane" : qUnion([Q1])});
        }
    });
